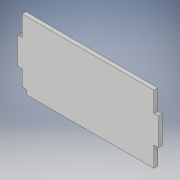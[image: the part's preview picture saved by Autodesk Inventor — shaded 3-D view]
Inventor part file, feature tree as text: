
AUTODESK INVENTOR PART (.ipt)
format: ipt  version: 2018 (Build 220112000, 112)  size: 105,984 bytes
history: native  units: in
note: dims shown in document units (in); Inventor stores cm internally (conversion verified against a paired STEP export)
features: extrude x2, sketch x2
ambient origin geometry x8: Origin, YZ Plane, XZ Plane, XY Plane, X Axis, Y Axis, Z Axis, Center Point
bodies: Solid1 (feature_tree)
feature tree (4):
  extrude  "Extrusion1"  Depth=0.2188in TaperAngle=0.0deg
  extrude  "Extrusion2"  [1 undecoded]
  sketch  "Sketch1"  dims[d0=7.25in d8=0.2188in d9=0.0in]
  sketch  "Sketch2"  dims[d10=0.25in d11=0.0in]
note: 1 required parameter value undecoded (feature->parameter linkage not recoverable at this tier; creation-order binding heuristic only, values carry confidence <= 0.55)
